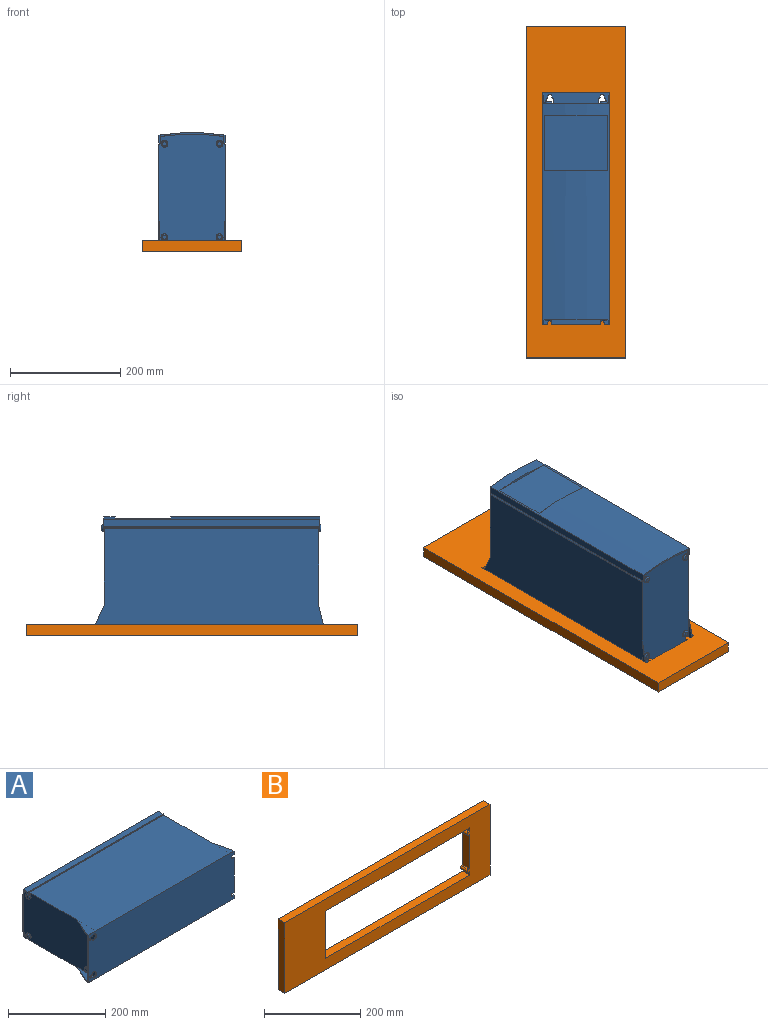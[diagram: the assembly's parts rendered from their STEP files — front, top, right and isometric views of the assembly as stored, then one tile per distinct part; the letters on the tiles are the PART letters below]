
ASSEMBLY  parts=2 mates=1
PART A: 78 faces, bbox 423x215x120 mm
  f0: plane 112.86x4mm, normal (1,0,0), area 301.2mm2, adj f2,f11
  f1: plane 112.86x4mm, normal (-1,0,0), area 301.2mm2, adj f2,f11
  f2: plane 112.85x101mm, normal (0,1,0), area 11398.2mm2, adj f0,f1,f11
  f3: plane 7.62x7.62mm, normal (1,0,0), area 45.6mm2, adj f16
  f4: plane 7.62x7.62mm, normal (1,0,0), area 45.6mm2, adj f17
  f5: plane 7.62x7.62mm, normal (1,0,0), area 45.6mm2, adj f18
  f6: plane 7.62x7.62mm, normal (1,0,0), area 45.6mm2, adj f19
  f7: plane 392.51x2.54mm, normal (0,-1,0), area 997mm2, adj f9,f20,f21,f23
  f8: plane 392.51x2.54mm, normal (0,-1,0), area 997mm2, adj f10,f21,f22,f23
  f9: plane 392.51x13.47mm, normal (0,0,-1), area 5288.9mm2, adj f7,f11,f21,f23
  f10: plane 392.51x13.47mm, normal (0,0,1), area 5288.9mm2, adj f8,f11,f21,f23
  f11: cylinder r=400mm len=392.51mm, axis (1,0,0), area 35843.8mm2, adj f0,f1,f2,f9,f10,f21,f23
  f12: plane 7.62x7.62mm, normal (-1,0,0), area 45.6mm2, adj f24
  f13: plane 7.62x7.62mm, normal (-1,0,0), area 45.6mm2, adj f25
  f14: plane 7.62x7.62mm, normal (-1,0,0), area 45.6mm2, adj f26
  f15: plane 7.62x7.62mm, normal (-1,0,0), area 45.6mm2, adj f27
  f16: torus R=3.81mm, axis (1,0,0), area 136mm2, adj f3,f29
  f17: torus R=3.81mm, axis (1,0,0), area 136mm2, adj f4,f30
  f18: torus R=3.81mm, axis (1,0,0), area 136mm2, adj f5,f31
  f19: torus R=3.81mm, axis (1,0,0), area 136mm2, adj f6,f32
  f20: plane 392.51x11.28mm, normal (0,0,1), area 4429.4mm2, adj f7,f21,f23,f34
  f21: plane 120x18mm, normal (-1,0,0), area 362.3mm2, adj f7,f8,f9,f10,f11,f20,f22,f34
  f22: plane 392.51x11.28mm, normal (0,0,-1), area 4429.4mm2, adj f8,f21,f23,f34
  f23: plane 120x18mm, normal (1,0,0), area 362.3mm2, adj f7,f8,f9,f10,f11,f20,f22,f34
  f24: torus R=3.81mm, axis (1,0,0), area 136mm2, adj f12,f36
  f25: torus R=3.81mm, axis (1,0,0), area 136mm2, adj f13,f37
  f26: torus R=3.81mm, axis (1,0,0), area 136mm2, adj f14,f38
  f27: torus R=3.81mm, axis (1,0,0), area 136mm2, adj f15,f39
  f28: cylinder r=1.27mm len=390mm, axis (1,0,0), area 615mm2, adj f33,f45,f49,f52
  f29: cylinder r=6.35mm len=12.7mm, axis (1,0,0), area 50.7mm2, adj f16,f49
  f30: cylinder r=6.35mm len=12.7mm, axis (1,0,0), area 50.7mm2, adj f17,f49
  f31: cylinder r=6.35mm len=12.7mm, axis (1,0,0), area 50.7mm2, adj f18,f49
  f32: cylinder r=6.35mm len=12.7mm, axis (1,0,0), area 50.7mm2, adj f19,f49
  f33: plane 390x11.55mm, normal (0,0,-1), area 4503.6mm2, adj f28,f34,f49,f52
  f34: cylinder r=397.46mm len=392.51mm, axis (1,0,0), area 890.6mm2, adj f20,f21,f22,f23,f33,f35,f49,f52
  f35: plane 390x11.55mm, normal (0,0,1), area 4503.6mm2, adj f34,f40,f49,f52
  f36: cylinder r=6.35mm len=12.7mm, axis (1,0,0), area 50.7mm2, adj f24,f52
  f37: cylinder r=6.35mm len=12.7mm, axis (1,0,0), area 50.7mm2, adj f25,f52
  f38: cylinder r=6.35mm len=12.7mm, axis (1,0,0), area 50.7mm2, adj f26,f52
  f39: cylinder r=6.35mm len=12.7mm, axis (1,0,0), area 50.7mm2, adj f27,f52
  f40: cylinder r=1.27mm len=390mm, axis (1,0,0), area 615mm2, adj f35,f49,f52,f53
  f41: plane 52.43x11.3mm, normal (0,0,-1), area 324.5mm2, adj f42,f49,f50,f57
  f42: plane 117x11.3mm, normal (0,1,0), area 1227.6mm2, adj f41,f43,f49,f57,f58,f59,f60,f61
  f43: plane 52.43x11.3mm, normal (0,0,1), area 324.5mm2, adj f42,f44,f49,f65
  f44: plane 47.43x11.3mm, normal (0.97,0.23,0), area 73.1mm2, adj f43,f49,f65,f66
  f45: cylinder r=3.94mm len=390mm, axis (1,0,0), area 1388.2mm2, adj f28,f49,f52,f66
  f46: plane 47.84x21.7mm, normal (-0.91,0.41,0), area 78.8mm2, adj f47,f52,f66,f67
  f47: plane 52.84x21.7mm, normal (0,0,1), area 627.5mm2, adj f46,f52,f56,f67
  f48: plane 52.84x21.7mm, normal (0,0,-1), area 627.5mm2, adj f51,f52,f56,f67
  f49: plane 210.96x120mm, normal (1,0,0), area 24383mm2, adj f28,f29,f30,f31,f32,f33,f34,f35
  f50: plane 47.43x11.3mm, normal (0.97,0.23,0), area 73.1mm2, adj f41,f49,f57,f68
  f51: plane 47.84x21.7mm, normal (-0.91,0.41,0), area 78.8mm2, adj f48,f52,f67,f68
  f52: plane 210.96x120mm, normal (-1,0,0), area 24382mm2, adj f28,f33,f34,f35,f36,f37,f38,f39
  f53: cylinder r=3.94mm len=390mm, axis (1,0,0), area 1388.2mm2, adj f40,f49,f52,f68
  f54: plane 8.13x1.3mm, normal (0,-1,0), area 7.2mm2, adj f52,f69
  f55: plane 8.13x1.3mm, normal (0,-1,0), area 7.2mm2, adj f52,f75
  f56: plane 117x21.7mm, normal (0,1,0), area 2174.6mm2, adj f47,f48,f52,f67,f69,f70,f71,f72
  f57: plane 9x6.5mm, normal (1,0,0), area 21mm2, adj f41,f42,f50,f58,f68,f77
  f58: plane 4x1.5mm, normal (0,0,-1), area 6mm2, adj f42,f57,f59,f77
  f59: cylinder r=3.5mm len=7mm, axis (0,1,0), area 16.5mm2, adj f42,f58,f60,f77
  f60: plane 4x1.5mm, normal (0,0,1), area 6mm2, adj f42,f59,f61,f77
  f61: plane 88x1.5mm, normal (1,0,0), area 132mm2, adj f42,f60,f62,f77
  f62: plane 4x1.5mm, normal (0,0,-1), area 6mm2, adj f42,f61,f63,f77
  f63: cylinder r=3.5mm len=7mm, axis (0,1,0), area 16.5mm2, adj f42,f62,f64,f77
  f64: plane 4x1.5mm, normal (0,0,1), area 6mm2, adj f42,f63,f65,f77
  f65: plane 9x6.5mm, normal (1,0,0), area 21mm2, adj f42,f43,f44,f64,f66,f77
  f66: plane 423x193.22mm, normal (0,0,-1), area 76358.9mm2, adj f44,f45,f46,f49,f52,f65,f67,f77
  f67: plane 120x6.5mm, normal (-1,0,0), area 195mm2, adj f46,f47,f48,f51,f56,f66,f68,f77
  f68: plane 423x193.22mm, normal (0,0,1), area 76358.9mm2, adj f49,f50,f51,f52,f53,f57,f67,f77
  f69: cylinder r=7mm len=14mm, axis (0,1,0), area 55mm2, adj f54,f56,f70,f72,f77
  f70: plane 2.94x1.5mm, normal (0,0,-1), area 4.4mm2, adj f56,f69,f71,f77
  f71: cylinder r=3.5mm len=7mm, axis (0,1,0), area 16.5mm2, adj f56,f70,f72,f77
  f72: plane 2.94x1.5mm, normal (0,0,1), area 4.4mm2, adj f56,f69,f71,f77
  f73: cylinder r=3.5mm len=7mm, axis (0,1,0), area 16.5mm2, adj f56,f74,f76,f77
  f74: plane 2.94x1.5mm, normal (0,0,1), area 4.4mm2, adj f56,f73,f75,f77
  f75: cylinder r=7mm len=14mm, axis (0,1,0), area 55mm2, adj f55,f56,f74,f76,f77
  f76: plane 2.94x1.5mm, normal (0,0,-1), area 4.4mm2, adj f56,f73,f75,f77
  f77: plane 423x120mm, normal (0,-1,0), area 50284.9mm2, adj f57,f58,f59,f60,f61,f62,f63,f64
PART B: 18 faces, bbox 603x20x180 mm
  f0: plane 120x20mm, normal (1,0,0), area 2400mm2, adj f1,f15,f16,f17
  f1: plane 423x20mm, normal (0,0,-1), area 8460mm2, adj f0,f2,f16,f17
  f2: plane 20x9mm, normal (-1,0,0), area 180mm2, adj f1,f3,f16,f17
  f3: plane 20x4mm, normal (0,0,1), area 80mm2, adj f2,f4,f16,f17
  f4: extruded ~20x7mm, area 220mm2, adj f3,f5,f16,f17
  f5: plane 20x4mm, normal (0,0,-1), area 80mm2, adj f4,f6,f16,f17
  f6: plane 88x20mm, normal (-1,0,0), area 1760mm2, adj f5,f7,f16,f17
  f7: plane 20x4mm, normal (0,0,1), area 80mm2, adj f6,f8,f16,f17
  f8: extruded ~20x7mm, area 220mm2, adj f7,f9,f16,f17
  f9: plane 20x4mm, normal (0,0,-1), area 80mm2, adj f8,f10,f16,f17
  f10: plane 20x9mm, normal (-1,0,0), area 180mm2, adj f9,f15,f16,f17
  f11: plane 603x20mm, normal (0,0,-1), area 12060mm2, adj f12,f14,f16,f17
  f12: plane 180x20mm, normal (1,0,0), area 3600mm2, adj f11,f13,f16,f17
  f13: plane 603x20mm, normal (0,0,1), area 12060mm2, adj f12,f14,f16,f17
  f14: plane 180x20mm, normal (-1,0,0), area 3600mm2, adj f11,f13,f16,f17
  f15: plane 423x20mm, normal (0,0,1), area 8460mm2, adj f0,f10,f16,f17
  f16: plane 603x180mm, normal (0,1,0), area 57876.9mm2, adj f0,f1,f2,f3,f4,f5,f6,f7
  f17: plane 603x180mm, normal (0,-1,0), area 57876.9mm2, adj f0,f1,f2,f3,f4,f5,f6,f7
PLACE A rot(axis=(0.58,-0.58,-0.58),120deg) t=(2.32,-160.16,-30.12)mm
PLACE B rot(axis=(0.58,-0.58,-0.58),120deg) t=(2.32,-160.16,-30.12)mm
MATE fastened B.f17 <-> A.f77  axis (0,0,-1) through (-57.68,51.34,-30.12)mm
